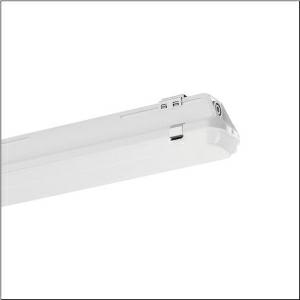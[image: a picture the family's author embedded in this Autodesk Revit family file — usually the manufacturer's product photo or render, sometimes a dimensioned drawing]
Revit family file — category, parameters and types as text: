
# Revit family: monsun_r__11_51fp10ep460l_92c6
name_source: partatom
category: Lighting Fixtures
units: mm (PartAtom-declared; Revit-internal decimal feet)

## family parameters
Cut with Voids When Loaded = No
Host = Face
Light Source = No
Part Type = Normal
Room Calculation Point = No
Round Connector Dimension = Use Diameter
Shared = No

## types (1)
- --- (1 x LED, 6050 lm, 31.5 W, 4000K)
    Apparent Load = 32 VA
    CIE Flux Codes = 47 77 93 94 100
    Color Rendering = 80
    Color Temperature = 4000K
    Default Elevation = 1800 mm
    Description = Monsun® 11, damp-proof luminaire, chain hanger, primary optical cover: enclosure, of PMMA, light emission: direct distribution, primary light characteristic: symmetric, installation type: suspended mounting, surface-mounted, horizontal mounting, vertical mounting, LED, rated luminous flux: 6.050lm, luminous efficacy: 192lm/W, light colour: 840, colour temperature: 4000K, control gear: DALI 2, with terminal, 5-pole, max. 2.5mm², mains connection: 220..240V, AC, 50/60Hz, rated input power: 32W, luminaire housing, of glass-fibre reinforced polyester, uncoated, bright grey, incl. chain hanger, length: 1.590mm, width: 90mm, height: 88mm, clip for enclosure, of stainless steel (V2A), ceiling mounting element, of stainless steel (V2A), chain hanger, of stainless steel (V2A), protection rating (complete): IP66, insulation class (complete): insulation class I (protective earthing), certification: CE, ENEC, VDE, UKCA, protection symbol: D, impact resistance: IK04, permissible operating ambient temperature: -25..+40°C, standard: EN 50419, EN 60598-2-1, corresponds to IFS (International Featured Standards) requirements for safety and quality in the food industry, for indoor or canopied outdoor use, no direct snow, no direct sun, no direct rain, LABS conformity tested according to VDMA 24364:2018-05, contact your sales advisor before using the luminaires in applications with unclear chemical exposure, large temperature fluctuations or condensation-forming humidity, packaging unit: 1 piece
    Height = 89 mm
    Lamp = 1 x LED
    Lamp Light Flux = 6050 lm
    Lamp Power = 31.5 W
    Lamp count = 1
    Length = 1590 mm
    Luminous efficacy = 192 lm/W
    Manufacturer = Siteco
    ModVariant = No
    Model = 51FP10EP460L
    Mounting Place = Ceiling
    Mounting Type = Surface mounted
    Number of Poles = 1
    OnlyDefault = Yes
    Power Factor = 1
    Product Name = Monsun® 11
    Product group = damp-proof luminaire
    ProductGroupID = 301
    Protection Class = Protection class I
    Protection Degree = IP 66
    RLX_Detail_Level = 1
    RLX_Emergency_Light_Flux = 0 lm
    RLX_Emergency_Type = 0
    RLX_Emergency_Type_DB = No
    RlxData = <blob elided: 92193 chars, md5=6d4a4912>
    Socket = socket
    Standby Power = 0 W
    System Light Flux = 6050 lm
    System Power = 32 W
    Type Comments = factory setting: luminous flux: 100 % | dim-lin: 254 | 219 mA
    Type Image = l_1349237.jpg
    URL = http://relux.com
    VarID = @adj_037791
    Voltage = 0 V
    Weight = 0.00 kg
    Width = 90 mm

## geometry (parser evidence)
native form markers: Blend x4, Sweep x13
no freeform markers — native parametric forms only
